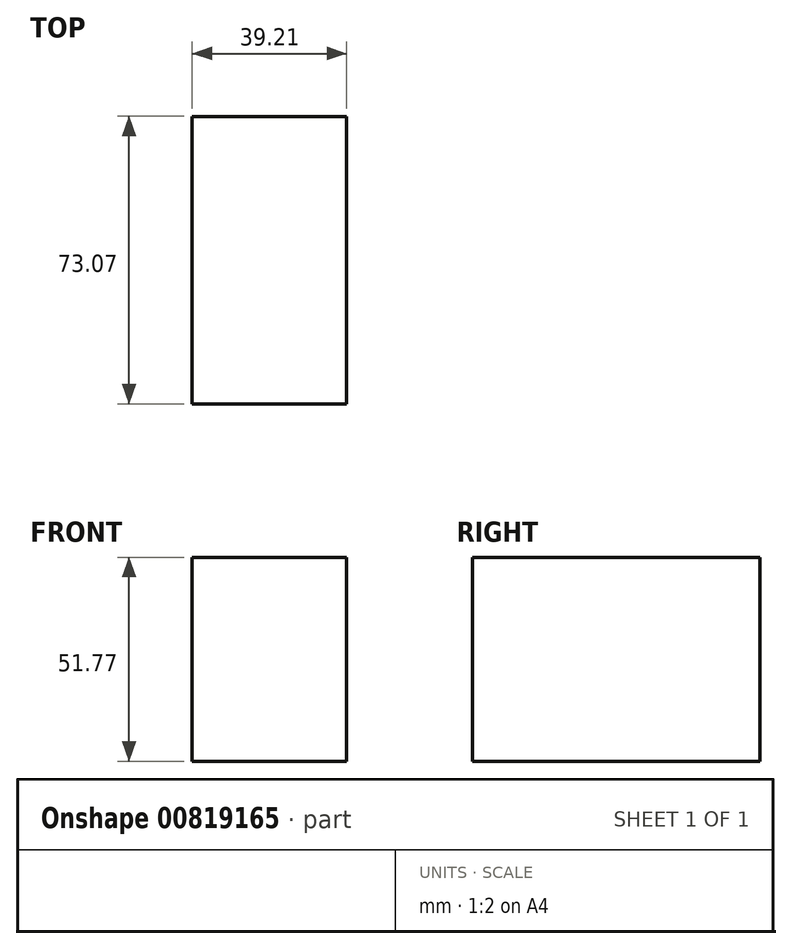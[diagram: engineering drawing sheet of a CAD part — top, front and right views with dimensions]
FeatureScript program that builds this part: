
annotation { "Feature Type Name" : "Feature", "Feature Type Description" : "" }
export const myFeature = defineFeature(function(context is Context, id is Id, definition is map)
    precondition{}
    {
        {
            var Q0;
            Q0=qCreatedBy(makeId("Right.planeOp"),FACE);
            var sketch = newSketch(context, id + "F0", { "sketchPlane" : qUnion([Q0])});
            skLineSegment(sketch, "E0.bottom", {"start": v(0, 0) * mm, "end": v(73.07, 0) * mm});
            skLineSegment(sketch, "E0.top", {"start": v(0, -51.77) * mm, "end": v(73.07, -51.77) * mm});
            skLineSegment(sketch, "E0.left", {"start": v(0, 0) * mm, "end": v(0, -51.77) * mm});
            skLineSegment(sketch, "E0.right", {"start": v(73.07, 0) * mm, "end": v(73.07, -51.77) * mm});
            skSolve(sketch);
        }
        {
            var Q0;
            Q0=sQuery(id+"F0.wireOp",EDGE,"E0.left");
            var Q1;
            Q1=sQuery(id+"F0.wireOp",EDGE,"E0.right");
            var Q2;
            Q2=sQuery(id+"F0.wireOp",EDGE,"E0.bottom");
            var Q3;
            Q3=sQuery(id+"F0.wireOp",EDGE,"E0.top");
            extrude(context, id + "F1", {"bodyType" : ToolBodyType.SURFACE, "surfaceEntities" : qUnion([Q0, Q1, Q2, Q3]), "depth" : 39.2 * mm, "offsetDistance" : 25.4 * mm});
        }
    });
